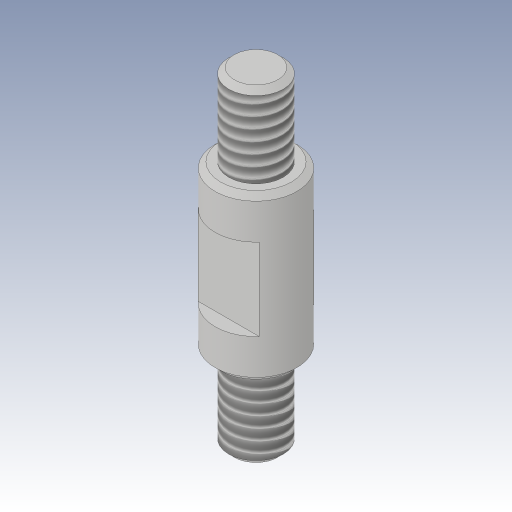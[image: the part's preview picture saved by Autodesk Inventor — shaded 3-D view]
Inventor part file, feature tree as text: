
AUTODESK INVENTOR PART (.ipt)
format: ipt  version: 2023.3 (Build 273359000, 359)  size: 180,224 bytes
history: native  units: in
note: dims shown in document units (in); Inventor stores cm internally (conversion verified against a paired STEP export)
features: thread x2, sketch x2, revolve x1, chamfer x1, extrude x1
ambient origin geometry x8: Origin, YZ Plane, XZ Plane, XY Plane, X Axis, Y Axis, Z Axis, Center Point
bodies: Body1 (feature_tree)
feature tree (7):
  revolve  "Umdrehung1"
  chamfer  "Fase1"  Distance=0.2362in
  thread  "Gewinde1"  [1 undecoded]
  thread  "Gewinde2"  [1 undecoded]
  extrude  "Extrusion3"  Depth=0.0787in
  sketch  "Skizze3"  dims[d4=0.1181in]
  sketch  "Skizze4"  dims[d5=0.4724in d6=0.2362in d7=0.1181in d8=0.0787in d9=0.0787in d10=90.0deg d11=0.0079in d12=0.0787in d13=45.0deg d14=0.1969in d15=0.0in d16=0.1969in d17=0.0in d18=0.1181in d19=0.0197in d20=0.0in d21=0.0in]
note: 2 required parameter values undecoded (feature->parameter linkage not recoverable at this tier; creation-order binding heuristic only, values carry confidence <= 0.55)
